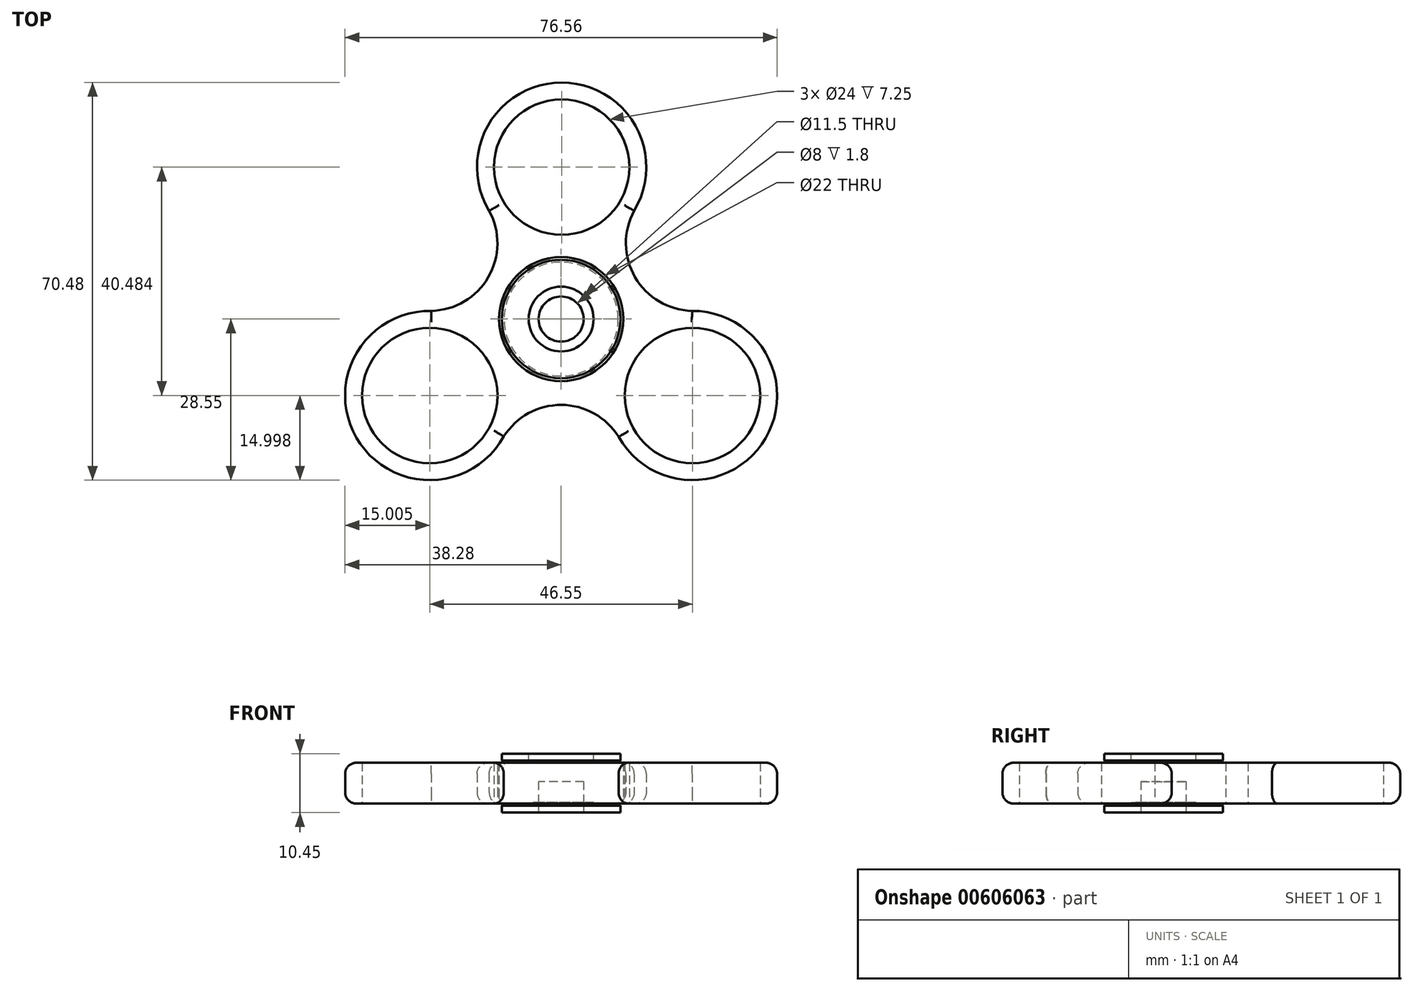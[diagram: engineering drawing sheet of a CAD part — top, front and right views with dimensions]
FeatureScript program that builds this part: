
annotation { "Feature Type Name" : "Feature", "Feature Type Description" : "" }
export const myFeature = defineFeature(function(context is Context, id is Id, definition is map)
    precondition{}
    {
        {
            var Q0;
            Q0=qCreatedBy(makeId("Top.planeOp"),FACE);
            var sketch = newSketch(context, id + "F0", { "sketchPlane" : qUnion([Q0])});
            skCircle(sketch, "E0", {"center": v(0, 0) * mm, "radius": 11 * mm});
            skCircle(sketch, "E1", {"center": v(0.1, 26.93) * mm, "radius": 12 * mm});
            skArc(sketch, "E2", {"start": v(12.95, 19.2) * mm, "mid": v(0.1, 41.93) * mm, "end": v(-12.75, 19.2) * mm});
            skCircle(sketch, "E3", {"center": v(23.28, -13.55) * mm, "radius": 12 * mm});
            skArc(sketch, "E4", {"start": v(10.2, -20.89) * mm, "mid": v(36.24, -21.1) * mm, "end": v(23.2, 1.45) * mm});
            skCircle(sketch, "E5", {"center": v(-23.28, -13.55) * mm, "radius": 12 * mm});
            skArc(sketch, "E6", {"start": v(-23, 1.45) * mm, "mid": v(-36.27, -21.05) * mm, "end": v(-10.15, -20.81) * mm});
            skArc(sketch, "E7", {"start": v(-23, 1.45) * mm, "mid": v(-12.9, 7.44) * mm, "end": v(-12.75, 19.2) * mm});
            skArc(sketch, "E8", {"start": v(12.95, 19.2) * mm, "mid": v(13.09, 7.44) * mm, "end": v(23.2, 1.45) * mm});
            skArc(sketch, "E9", {"start": v(10.2, -20.89) * mm, "mid": v(0.04, -15.22) * mm, "end": v(-10.15, -20.81) * mm});
            skCircle(sketch, "E10", {"center": v(0, 0) * mm, "radius": 26.93 * mm, "construction": true});
            skSolve(sketch);
        }
        {
            var Q0;
            Q0=makeQuery(id+"F0.imprint","IMPRINT",FACE,{"disambiguationData":[TD([[makeQuery(id+"F0.imprint","IMPRINT",EDGE,{"derivedFrom":sQuery(id+"F0.wireOp",EDGE,"E0")}),-1.0]])]});
            extrude(context, id + "F1", {"entities" : qUnion([Q0]), "depth" : 7.25 * mm, "offsetDistance" : 25 * mm});
        }
        {
            var Q0;
            Q0=makeQuery(id+"F1.opExtrude","CAP_EDGE",EDGE,{"disambiguationData":[OSD([sQuery(id+"F0.wireOp",EDGE,"E2")])],"isStart":false});
            var Q1;
            Q1=makeQuery(id+"F1.opExtrude","CAP_EDGE",EDGE,{"disambiguationData":[OSD([sQuery(id+"F0.wireOp",EDGE,"E4")])],"isStart":false});
            var Q2;
            Q2=makeQuery(id+"F1.opExtrude","CAP_EDGE",EDGE,{"disambiguationData":[OSD([sQuery(id+"F0.wireOp",EDGE,"E6")])],"isStart":false});
            var Q3;
            Q3=makeQuery(id+"F1.opExtrude","CAP_EDGE",EDGE,{"disambiguationData":[OSD([sQuery(id+"F0.wireOp",EDGE,"E6")])],"isStart":true});
            var Q4;
            Q4=makeQuery(id+"F1.opExtrude","CAP_EDGE",EDGE,{"disambiguationData":[OSD([sQuery(id+"F0.wireOp",EDGE,"E2")])],"isStart":true});
            var Q5;
            Q5=makeQuery(id+"F1.opExtrude","CAP_EDGE",EDGE,{"disambiguationData":[OSD([sQuery(id+"F0.wireOp",EDGE,"E4")])],"isStart":true});
            fillet(context, id + "F2", {"entities" : qUnion([Q0, Q1, Q2, Q3, Q4, Q5]), "radius" : 2 * mm, "tangentPropagation" : true, "allowEdgeOverflow" : false});
        }
        {
            var Q0;
            Q0=qCreatedBy(makeId("Top.planeOp"),FACE);
            cPlane(context, id + "F3", {"entities" : qUnion([Q0]), "cplaneType" : CPlaneType.OFFSET, "offset" : 1.6 * mm, "oppositeDirection" : true, "width" : 150 * mm, "height" : 150 * mm});
        }
        {
            var Q0;
            Q0=qCreatedBy(id+"F3.planeOp",FACE);
            var sketch = newSketch(context, id + "F4", { "sketchPlane" : qUnion([Q0])});
            skCircle(sketch, "E11", {"center": v(0, 0) * mm, "radius": 10.5 * mm});
            skCircle(sketch, "E12", {"center": v(0, 0) * mm, "radius": 4 * mm});
            skCircle(sketch, "E13", {"center": v(0, 0) * mm, "radius": 5.75 * mm});
            skSolve(sketch);
        }
        {
            var Q0;
            Q0=makeQuery(id+"F4.imprint","IMPRINT",FACE,{"disambiguationData":[TD([[makeQuery(id+"F4.imprint","IMPRINT",EDGE,{"derivedFrom":sQuery(id+"F4.wireOp",EDGE,"E11")}),1.0]])]});
            extrude(context, id + "F5", {"entities" : qUnion([Q0]), "depth" : 1.6 * mm, "offsetDistance" : 25 * mm});
        }
        {
            var Q0;
            Q0=makeQuery(id+"F4.imprint","IMPRINT",FACE,{"disambiguationData":[TD([[makeQuery(id+"F4.imprint","IMPRINT",EDGE,{"derivedFrom":sQuery(id+"F4.wireOp",EDGE,"E12")}),1.0]])]});
            extrude(context, id + "F6", {"entities" : qUnion([Q0]), "operationType" : NewBodyOperationType.ADD, "depth" : 5.5 * mm, "offsetDistance" : 25 * mm});
        }
        {
            var Q0;
            Q0=makeQuery(id+"F5.opExtrude","CAP_EDGE",EDGE,{"disambiguationData":[OSD([sQuery(id+"F4.wireOp",EDGE,"E11")])],"isStart":false});
            chamfer(context, id + "F7", {"entities" : qUnion([Q0]), "width" : .4 * mm, "tangentPropagation" : true});
        }
        {
            var Q0;
            Q0=makeQuery(id+"F4.imprint","IMPRINT",FACE,{"disambiguationData":[TD([[makeQuery(id+"F4.imprint","IMPRINT",EDGE,{"derivedFrom":sQuery(id+"F4.wireOp",EDGE,"E12")}),-1.0]])]});
            extrude(context, id + "F8", {"entities" : qUnion([Q0]), "depth" : 1.8 * mm, "offsetDistance" : 25 * mm});
        }
        {
            var Q0;
            Q0=qCreatedBy(makeId("Top.planeOp"),FACE);
            cPlane(context, id + "F9", {"entities" : qUnion([Q0]), "cplaneType" : CPlaneType.OFFSET, "offset" : 3.62 * mm, "width" : 150 * mm, "height" : 150 * mm});
        }
        {
            var Q0;
            Q0=makeQuery(id+"F5.opExtrude","SWEPT_BODY",BODY,{"disambiguationData":[OSD([sQuery(id+"F4.wireOp",EDGE,"E11"),sQuery(id+"F4.wireOp",EDGE,"E13")])]});
            var Q1;
            Q1=qCreatedBy(id+"F9.planeOp",FACE);
            mirror(context, id + "F10", {"operationType" : NewBodyOperationType.ADD, "entities" : qUnion([Q0]), "mirrorPlane" : qUnion([Q1])});
        }
    });
